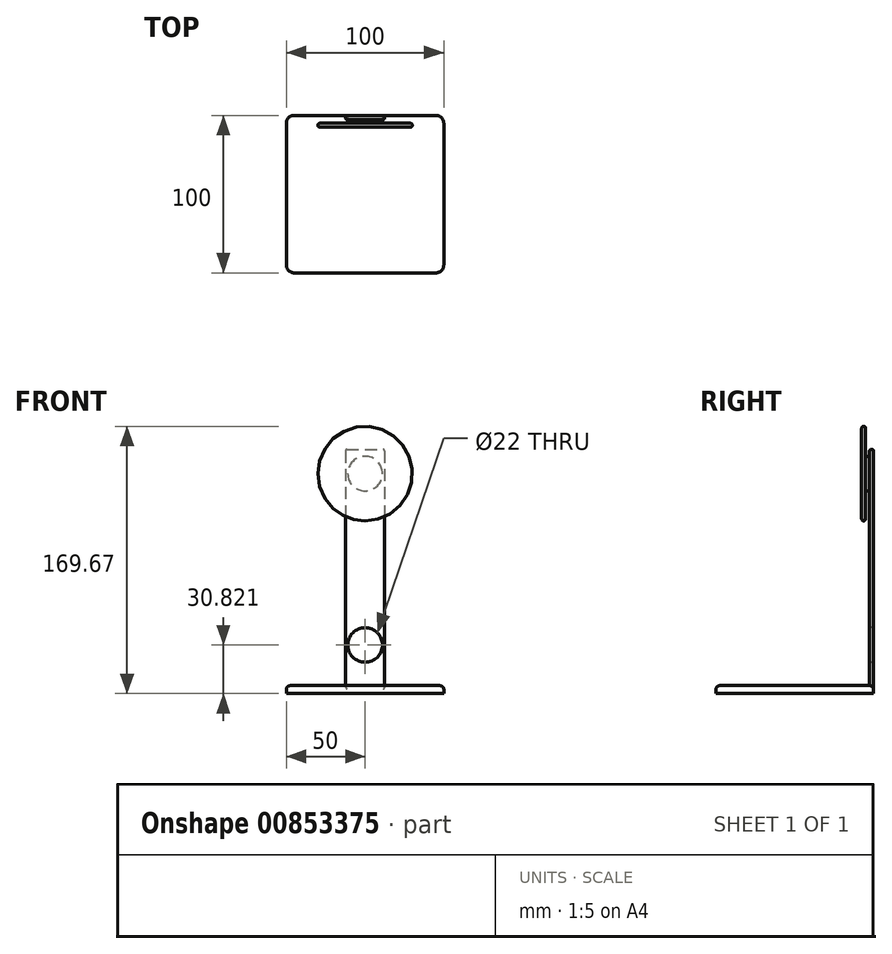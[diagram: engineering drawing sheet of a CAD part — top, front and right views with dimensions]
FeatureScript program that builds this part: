
annotation { "Feature Type Name" : "Feature", "Feature Type Description" : "" }
export const myFeature = defineFeature(function(context is Context, id is Id, definition is map)
    precondition{}
    {
        {
            var Q0;
            Q0=qCreatedBy(makeId("Top.planeOp"),FACE);
            var sketch = newSketch(context, id + "F0", { "sketchPlane" : qUnion([Q0])});
            skLineSegment(sketch, "E0", {"start": v(-100, 0) * mm, "end": v(100, 0) * mm, "construction": true});
            skLineSegment(sketch, "E1", {"start": v(0, -100) * mm, "end": v(0, 100) * mm, "construction": true});
            skLineSegment(sketch, "E2", {"start": v(-50, -50) * mm, "end": v(50, -50) * mm});
            skLineSegment(sketch, "E3", {"start": v(-50, -50) * mm, "end": v(-50, 50) * mm});
            skLineSegment(sketch, "E4", {"start": v(-50, 50) * mm, "end": v(50, 50) * mm});
            skLineSegment(sketch, "E5", {"start": v(50, 50) * mm, "end": v(50, -50) * mm});
            skSolve(sketch);
        }
        {
            var Q0;
            Q0=makeQuery(id+"F0.imprint","IMPRINT",FACE,{"disambiguationData":[TD([[makeQuery(id+"F0.imprint","IMPRINT",EDGE,{"derivedFrom":sQuery(id+"F0.wireOp",EDGE,"E2")}),1.0]])]});
            extrude(context, id + "F1", {"entities" : qUnion([Q0]), "depth" : 5 * mm, "offsetDistance" : 25 * mm});
        }
        {
            var Q0;
            Q0=makeQuery(id+"F1.opExtrude","SWEPT_EDGE",EDGE,{"disambiguationData":[OSD([sQuery(id+"F0.wireOp",EDGE,"E4"),sQuery(id+"F0.wireOp",EDGE,"E5")])]});
            var Q1;
            Q1=makeQuery(id+"F1.opExtrude","SWEPT_EDGE",EDGE,{"disambiguationData":[OSD([sQuery(id+"F0.wireOp",EDGE,"E3"),sQuery(id+"F0.wireOp",EDGE,"E4")])]});
            var Q2;
            Q2=makeQuery(id+"F1.opExtrude","SWEPT_EDGE",EDGE,{"disambiguationData":[OSD([sQuery(id+"F0.wireOp",EDGE,"E2"),sQuery(id+"F0.wireOp",EDGE,"E3")])]});
            var Q3;
            Q3=makeQuery(id+"F1.opExtrude","SWEPT_EDGE",EDGE,{"disambiguationData":[OSD([sQuery(id+"F0.wireOp",EDGE,"E2"),sQuery(id+"F0.wireOp",EDGE,"E5")])]});
            fillet(context, id + "F2", {"entities" : qUnion([Q0, Q1, Q2, Q3]), "radius" : 5 * mm, "tangentPropagation" : true, "allowEdgeOverflow" : false});
        }
        {
            var Q0;
            Q0=makeQuery(id+"F1.opExtrude","CAP_FACE",FACE,{"disambiguationData":[OSD([sQuery(id+"F0.wireOp",EDGE,"E2"),sQuery(id+"F0.wireOp",EDGE,"E3"),sQuery(id+"F0.wireOp",EDGE,"E4"),sQuery(id+"F0.wireOp",EDGE,"E5")])],"isStart":false});
            var sketch = newSketch(context, id + "F3", { "sketchPlane" : qUnion([Q0])});
            skPoint(sketch, "E6.startSnap0", {"position": v(0, 50) * mm});
            skLineSegment(sketch, "E7", {"start": v(12.5, 50) * mm, "end": v(-12.5, 50) * mm});
            skLineSegment(sketch, "E8", {"start": v(-12.5, 50) * mm, "end": v(-12.5, 47.5) * mm});
            skLineSegment(sketch, "E9", {"start": v(-12.5, 47.5) * mm, "end": v(12.5, 47.5) * mm});
            skLineSegment(sketch, "E10", {"start": v(12.5, 47.5) * mm, "end": v(12.5, 50) * mm});
            skSolve(sketch);
        }
        {
            var Q0;
            Q0=makeQuery(id+"F3.imprint","IMPRINT",FACE,{"disambiguationData":[TD([[makeQuery(id+"F3.imprint","IMPRINT",EDGE,{"derivedFrom":sQuery(id+"F3.wireOp",EDGE,"E7")}),-1.0]])]});
            extrude(context, id + "F4", {"entities" : qUnion([Q0]), "operationType" : NewBodyOperationType.ADD, "depth" : 150 * mm, "offsetDistance" : 25 * mm});
        }
        {
            var Q0;
            Q0=makeQuery(id+"F1.opExtrude","CAP_EDGE",EDGE,{"disambiguationData":[OSD([sQuery(id+"F0.wireOp",EDGE,"E3")])],"isStart":false});
            fillet(context, id + "F5", {"entities" : qUnion([Q0]), "radius" : 2.5 * mm, "tangentPropagation" : true, "allowEdgeOverflow" : false});
        }
        {
            var Q0;
            Q0=makeQuery(id+"F4.opExtrude","SWEPT_EDGE",EDGE,{"disambiguationData":[OSD([sQuery(id+"F3.wireOp",EDGE,"E8"),sQuery(id+"F3.wireOp",EDGE,"E9")])]});
            var Q1;
            Q1=makeQuery(id+"F4.opExtrude","SWEPT_EDGE",EDGE,{"disambiguationData":[OSD([sQuery(id+"F0.wireOp",EDGE,"E4"),sQuery(id+"F3.wireOp",EDGE,"E7"),sQuery(id+"F3.wireOp",EDGE,"E8")])]});
            var Q2;
            Q2=makeQuery(id+"F4.opExtrude","SWEPT_EDGE",EDGE,{"disambiguationData":[OSD([sQuery(id+"F0.wireOp",EDGE,"E4"),sQuery(id+"F3.wireOp",EDGE,"E7"),sQuery(id+"F3.wireOp",EDGE,"E10")])]});
            var Q3;
            Q3=makeQuery(id+"F4.opExtrude","SWEPT_EDGE",EDGE,{"disambiguationData":[OSD([sQuery(id+"F3.wireOp",EDGE,"E9"),sQuery(id+"F3.wireOp",EDGE,"E10")])]});
            fillet(context, id + "F6", {"entities" : qUnion([Q0, Q1, Q2, Q3]), "radius" : 1 * mm, "tangentPropagation" : true, "allowEdgeOverflow" : false});
        }
        {
            var Q0;
            Q0=makeQuery(id+"F4.opExtrude","CAP_EDGE",EDGE,{"disambiguationData":[OSD([sQuery(id+"F3.wireOp",EDGE,"E7")])],"isStart":false});
            fillet(context, id + "F7", {"entities" : qUnion([Q0]), "radius" : 1 * mm, "tangentPropagation" : true, "allowEdgeOverflow" : false});
        }
        {
            var Q0;
            Q0=makeQuery(id+"F4.opExtrude","SWEPT_FACE",FACE,{"disambiguationData":[OSD([sQuery(id+"F3.wireOp",EDGE,"E9")])]});
            var sketch = newSketch(context, id + "F8", { "sketchPlane" : qUnion([Q0])});
            skLineSegment(sketch, "E11", {"start": v(0, 0) * mm, "end": v(0, 159.7) * mm, "construction": true});
            skCircle(sketch, "E12", {"center": v(0, 30.82) * mm, "radius": 11 * mm});
            skSolve(sketch);
        }
        {
            var Q0;
            Q0 = qSketchRegion(id + "F8", true);
            extrude(context, id + "F9", {"entities" : qUnion([Q0]), "operationType" : NewBodyOperationType.REMOVE, "oppositeDirection" : true, "depth" : 25 * mm, "offsetDistance" : 25 * mm});
        }
        {
            var Q0;
            Q0=makeQuery(id+"F4.opExtrude","SWEPT_FACE",FACE,{"disambiguationData":[OSD([sQuery(id+"F3.wireOp",EDGE,"E9")])]});
            var sketch = newSketch(context, id + "F10", { "sketchPlane" : qUnion([Q0])});
            skLineSegment(sketch, "E13", {"start": v(0, 139.67) * mm, "end": v(-72.98, 139.67) * mm, "construction": true});
            skLineSegment(sketch, "E14", {"start": v(-72.98, 139.67) * mm, "end": v(63.84, 139.67) * mm, "construction": true});
            skCircle(sketch, "E15", {"center": v(0, 139.67) * mm, "radius": 11 * mm});
            skSolve(sketch);
        }
        {
            var Q0;
            Q0 = qSketchRegion(id + "F10", true);
            extrude(context, id + "F11", {"entities" : qUnion([Q0]), "depth" : 2.5 * mm, "offsetDistance" : 25 * mm});
        }
        {
            var Q0;
            Q0=makeQuery(id+"F11.opExtrude","CAP_FACE",FACE,{"disambiguationData":[OSD([sQuery(id+"F10.wireOp",EDGE,"E15")])],"isStart":false});
            var sketch = newSketch(context, id + "F12", { "sketchPlane" : qUnion([Q0])});
            skCircle(sketch, "E16", {"center": v(0, 139.67) * mm, "radius": 30 * mm});
            skSolve(sketch);
        }
        {
            var Q0;
            Q0 = qSketchRegion(id + "F12", true);
            extrude(context, id + "F13", {"entities" : qUnion([Q0]), "operationType" : NewBodyOperationType.ADD, "depth" : 2.5 * mm, "offsetDistance" : 25 * mm});
        }
        {
            var Q0;
            Q0=makeQuery(id+"F13.opExtrude","CAP_EDGE",EDGE,{"disambiguationData":[OSD([sQuery(id+"F12.wireOp",EDGE,"E16")])],"isStart":false});
            fillet(context, id + "F14", {"entities" : qUnion([Q0]), "radius" : 1.25 * mm, "tangentPropagation" : true, "allowEdgeOverflow" : false});
        }
        {
            var Q0;
            Q0=makeQuery(id+"F13.opExtrude","CAP_EDGE",EDGE,{"disambiguationData":[OSD([sQuery(id+"F12.wireOp",EDGE,"E16")])],"isStart":true});
            fillet(context, id + "F15", {"entities" : qUnion([Q0]), "radius" : 1.25 * mm, "tangentPropagation" : true, "allowEdgeOverflow" : false});
        }
        {
            var Q0;
            Q0=makeQuery(id+"F11.opExtrude","CAP_EDGE",EDGE,{"disambiguationData":[OSD([sQuery(id+"F10.wireOp",EDGE,"E15")])],"isStart":false});
            var Q1;
            Q1=makeQuery(id+"F11.opExtrude","CAP_EDGE",EDGE,{"disambiguationData":[OSD([sQuery(id+"F10.wireOp",EDGE,"E15")])],"isStart":true});
            fillet(context, id + "F16", {"entities" : qUnion([Q0, Q1]), "radius" : 1.25 * mm, "tangentPropagation" : true, "allowEdgeOverflow" : false});
        }
    });
